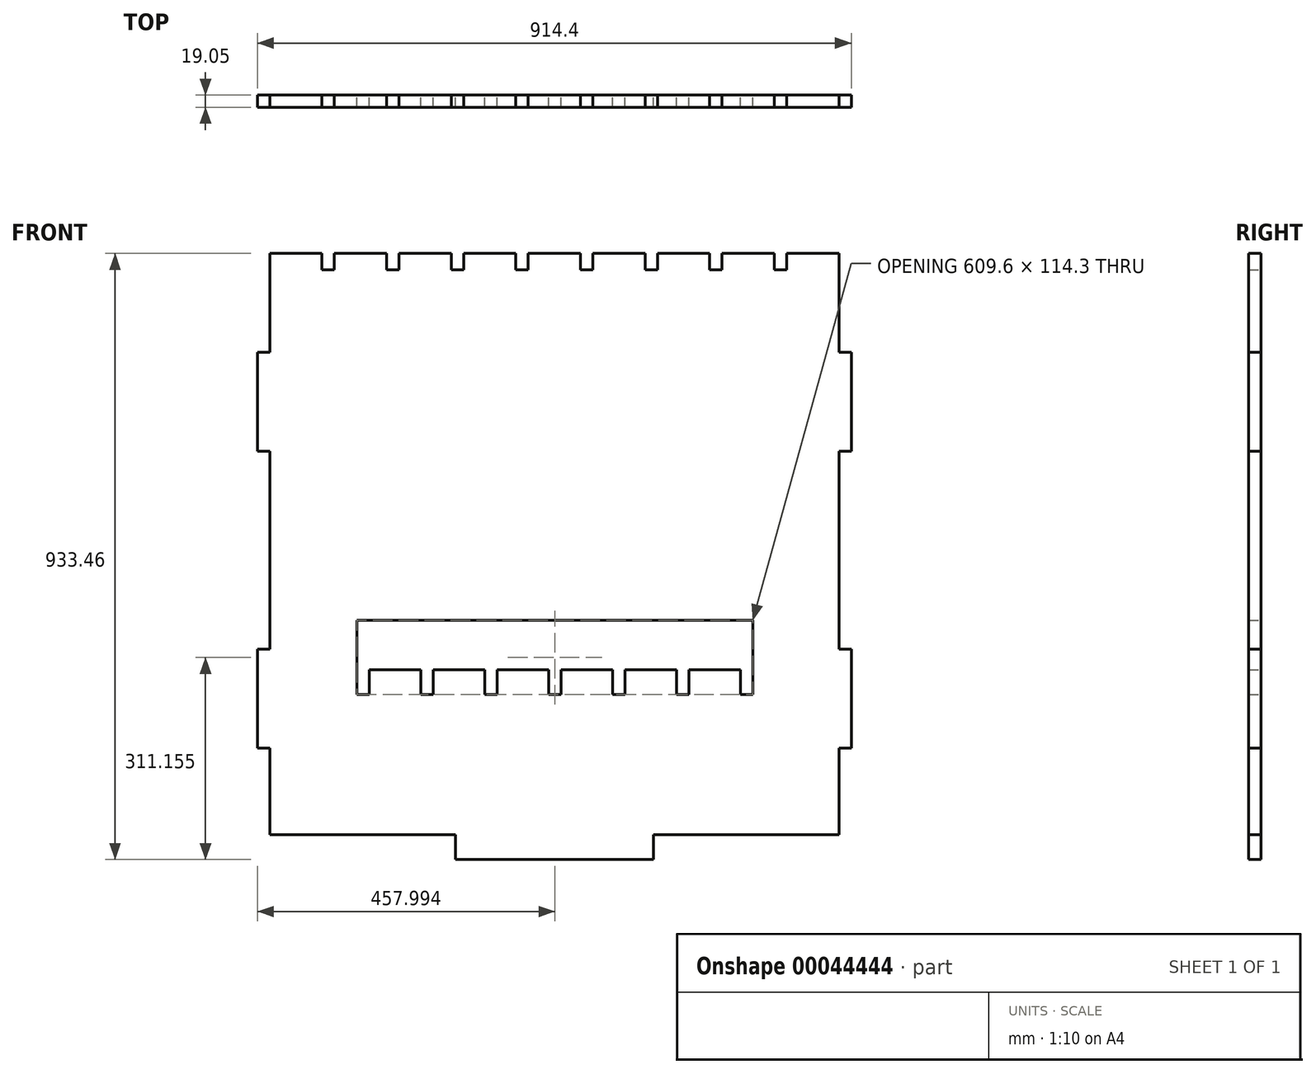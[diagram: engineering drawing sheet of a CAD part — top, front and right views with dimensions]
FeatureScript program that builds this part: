
annotation { "Feature Type Name" : "Feature", "Feature Type Description" : "" }
export const myFeature = defineFeature(function(context is Context, id is Id, definition is map)
    precondition{}
    {
        {
            var Q0;
            Q0=qCreatedBy(makeId("Front.planeOp"),FACE);
            var sketch = newSketch(context, id + "F0", { "sketchPlane" : qUnion([Q0])});
            skLineSegment(sketch, "E0.rect.bottom", {"start": v(-438.15, -447.68) * mm, "end": v(438.15, -447.67) * mm});
            skLineSegment(sketch, "E0.rect.top", {"start": v(-438.15, 447.67) * mm, "end": v(438.15, 447.68) * mm});
            skLineSegment(sketch, "E0.rect.left", {"start": v(-438.15, -447.68) * mm, "end": v(-438.15, 447.67) * mm});
            skLineSegment(sketch, "E0.rect.right", {"start": v(438.15, -447.67) * mm, "end": v(438.15, 447.68) * mm});
            skPoint(sketch, "E0.rect.middle", {"position": v(0, 0) * mm});
            skLineSegment(sketch, "E1.bottom", {"start": v(-304, -117.48) * mm, "end": v(305.6, -117.47) * mm});
            skLineSegment(sketch, "E1.left", {"start": v(-304, -117.48) * mm, "end": v(-304, -193.68) * mm});
            skLineSegment(sketch, "E1.right", {"start": v(305.6, -117.47) * mm, "end": v(305.6, -193.67) * mm});
            skLineSegment(sketch, "E2.bottom", {"start": v(-438.15, 295.27) * mm, "end": v(-457.2, 295.27) * mm});
            skLineSegment(sketch, "E2.top", {"start": v(-438.15, 142.87) * mm, "end": v(-457.2, 142.87) * mm});
            skLineSegment(sketch, "E2.left", {"start": v(-438.15, 295.27) * mm, "end": v(-438.15, 142.87) * mm});
            skLineSegment(sketch, "E2.right", {"start": v(-457.2, 295.27) * mm, "end": v(-457.2, 142.87) * mm});
            skLineSegment(sketch, "E3.bottom", {"start": v(-438.15, -161.93) * mm, "end": v(-457.2, -161.93) * mm});
            skLineSegment(sketch, "E3.top", {"start": v(-438.15, -314.33) * mm, "end": v(-457.2, -314.33) * mm});
            skLineSegment(sketch, "E3.left", {"start": v(-438.15, -161.93) * mm, "end": v(-438.15, -314.33) * mm});
            skLineSegment(sketch, "E3.right", {"start": v(-457.2, -161.93) * mm, "end": v(-457.2, -314.33) * mm});
            skLineSegment(sketch, "E4.bottom", {"start": v(-152.4, -447.68) * mm, "end": v(152.4, -447.67) * mm});
            skLineSegment(sketch, "E4.top", {"start": v(-152.4, -485.78) * mm, "end": v(152.4, -485.77) * mm});
            skLineSegment(sketch, "E4.left", {"start": v(-152.4, -447.68) * mm, "end": v(-152.4, -485.78) * mm});
            skLineSegment(sketch, "E5.MirrorCS", {"start": v(438.15, 142.88) * mm, "end": v(457.2, 142.88) * mm});
            skLineSegment(sketch, "E6.MirrorCS", {"start": v(438.15, 295.28) * mm, "end": v(457.2, 295.28) * mm});
            skLineSegment(sketch, "E7.MirrorCS", {"start": v(438.15, 295.27) * mm, "end": v(438.15, 142.87) * mm});
            skLineSegment(sketch, "E8.MirrorCS", {"start": v(457.2, 295.27) * mm, "end": v(457.2, 142.87) * mm});
            skLineSegment(sketch, "E9.MirrorCS", {"start": v(457.2, -161.93) * mm, "end": v(457.2, -314.33) * mm});
            skLineSegment(sketch, "E10.MirrorCS", {"start": v(438.15, -161.93) * mm, "end": v(438.15, -314.33) * mm});
            skLineSegment(sketch, "E11.MirrorCS", {"start": v(438.15, -161.92) * mm, "end": v(457.2, -161.92) * mm});
            skLineSegment(sketch, "E12.MirrorCS", {"start": v(438.15, -314.32) * mm, "end": v(457.2, -314.32) * mm});
            skLineSegment(sketch, "E13.MirrorCS", {"start": v(152.4, -447.68) * mm, "end": v(152.4, -485.78) * mm});
            skLineSegment(sketch, "E14.MirrorCS", {"start": v(152.4, -447.67) * mm, "end": v(-152.4, -447.68) * mm});
            skLineSegment(sketch, "E15.MirrorCS", {"start": v(152.4, -485.77) * mm, "end": v(-152.4, -485.78) * mm});
            skLineSegment(sketch, "E16.bottom", {"start": v(-205.58, -193.68) * mm, "end": v(-186.53, -193.68) * mm});
            skLineSegment(sketch, "E16.top", {"start": v(-205.58, -231.77) * mm, "end": v(-186.53, -231.77) * mm});
            skLineSegment(sketch, "E16.left", {"start": v(-205.58, -193.68) * mm, "end": v(-205.58, -231.78) * mm});
            skLineSegment(sketch, "E16.right", {"start": v(-186.53, -193.68) * mm, "end": v(-186.53, -231.78) * mm});
            skLineSegment(sketch, "E17.bottom", {"start": v(-107.16, -193.67) * mm, "end": v(-88.1, -193.67) * mm});
            skLineSegment(sketch, "E17.top", {"start": v(-107.16, -231.77) * mm, "end": v(-88.1, -231.77) * mm});
            skLineSegment(sketch, "E17.left", {"start": v(-107.16, -193.68) * mm, "end": v(-107.16, -231.78) * mm});
            skLineSegment(sketch, "E17.right", {"start": v(-88.1, -193.68) * mm, "end": v(-88.1, -231.78) * mm});
            skLineSegment(sketch, "E18.bottom", {"start": v(-8.73, -193.67) * mm, "end": v(10.32, -193.67) * mm});
            skLineSegment(sketch, "E18.top", {"start": v(-8.73, -231.77) * mm, "end": v(10.32, -231.77) * mm});
            skLineSegment(sketch, "E18.left", {"start": v(-8.73, -193.68) * mm, "end": v(-8.73, -231.78) * mm});
            skLineSegment(sketch, "E18.right", {"start": v(10.32, -193.68) * mm, "end": v(10.32, -231.78) * mm});
            skLineSegment(sketch, "E19.bottom", {"start": v(89.7, -193.67) * mm, "end": v(108.74, -193.67) * mm});
            skLineSegment(sketch, "E19.top", {"start": v(89.7, -231.77) * mm, "end": v(108.74, -231.77) * mm});
            skLineSegment(sketch, "E19.left", {"start": v(89.7, -193.68) * mm, "end": v(89.7, -231.78) * mm});
            skLineSegment(sketch, "E19.right", {"start": v(108.74, -193.68) * mm, "end": v(108.74, -231.78) * mm});
            skLineSegment(sketch, "E20.bottom", {"start": v(188.12, -193.67) * mm, "end": v(207.17, -193.67) * mm});
            skLineSegment(sketch, "E20.top", {"start": v(188.12, -231.77) * mm, "end": v(207.17, -231.77) * mm});
            skLineSegment(sketch, "E20.left", {"start": v(188.12, -193.67) * mm, "end": v(188.12, -231.78) * mm});
            skLineSegment(sketch, "E20.right", {"start": v(207.17, -193.67) * mm, "end": v(207.17, -231.78) * mm});
            skLineSegment(sketch, "E21", {"start": v(-304, -193.68) * mm, "end": v(305.6, -193.67) * mm});
            skLineSegment(sketch, "E22.top", {"start": v(40.22, 422.27) * mm, "end": v(59.27, 422.27) * mm});
            skLineSegment(sketch, "E23.right", {"start": v(-338.67, 447.67) * mm, "end": v(-338.67, 422.27) * mm});
            skLineSegment(sketch, "E24.left", {"start": v(139.7, 447.68) * mm, "end": v(139.7, 422.27) * mm});
            skLineSegment(sketch, "E24.top", {"start": v(139.7, 422.27) * mm, "end": v(158.75, 422.27) * mm});
            skLineSegment(sketch, "E24.right", {"start": v(158.75, 447.68) * mm, "end": v(158.75, 422.27) * mm});
            skLineSegment(sketch, "E25.top", {"start": v(338.67, 422.27) * mm, "end": v(357.72, 422.27) * mm});
            skLineSegment(sketch, "E26.left", {"start": v(-258.23, 447.67) * mm, "end": v(-258.23, 422.27) * mm});
            skLineSegment(sketch, "E22.right", {"start": v(59.27, 447.68) * mm, "end": v(59.27, 422.27) * mm});
            skLineSegment(sketch, "E27.top", {"start": v(239.18, 422.27) * mm, "end": v(258.23, 422.27) * mm});
            skLineSegment(sketch, "E28.top", {"start": v(-158.75, 422.27) * mm, "end": v(-139.7, 422.27) * mm});
            skLineSegment(sketch, "E26.top", {"start": v(-258.23, 422.27) * mm, "end": v(-239.18, 422.27) * mm});
            skLineSegment(sketch, "E22.left", {"start": v(40.22, 447.68) * mm, "end": v(40.22, 422.27) * mm});
            skLineSegment(sketch, "E23.top", {"start": v(-357.72, 422.27) * mm, "end": v(-338.67, 422.27) * mm});
            skLineSegment(sketch, "E25.left", {"start": v(338.67, 447.68) * mm, "end": v(338.67, 422.27) * mm});
            skLineSegment(sketch, "E26.right", {"start": v(-239.18, 447.68) * mm, "end": v(-239.18, 422.27) * mm});
            skLineSegment(sketch, "E29.right", {"start": v(-40.22, 447.68) * mm, "end": v(-40.22, 422.27) * mm});
            skLineSegment(sketch, "E27.left", {"start": v(239.18, 447.68) * mm, "end": v(239.18, 422.27) * mm});
            skLineSegment(sketch, "E28.left", {"start": v(-158.75, 447.68) * mm, "end": v(-158.75, 422.27) * mm});
            skLineSegment(sketch, "E29.top", {"start": v(-59.27, 422.27) * mm, "end": v(-40.22, 422.27) * mm});
            skLineSegment(sketch, "E23.left", {"start": v(-357.72, 447.67) * mm, "end": v(-357.72, 422.27) * mm});
            skLineSegment(sketch, "E25.right", {"start": v(357.72, 447.68) * mm, "end": v(357.72, 422.27) * mm});
            skLineSegment(sketch, "E29.left", {"start": v(-59.27, 447.68) * mm, "end": v(-59.27, 422.27) * mm});
            skLineSegment(sketch, "E27.right", {"start": v(258.23, 447.68) * mm, "end": v(258.23, 422.27) * mm});
            skLineSegment(sketch, "E28.right", {"start": v(-139.7, 447.68) * mm, "end": v(-139.7, 422.27) * mm});
            skLineSegment(sketch, "E30.bottom", {"start": v(-304, -193.68) * mm, "end": v(-284.96, -193.68) * mm});
            skLineSegment(sketch, "E30.top", {"start": v(-304, -231.78) * mm, "end": v(-284.96, -231.78) * mm});
            skLineSegment(sketch, "E30.left", {"start": v(-304, -193.68) * mm, "end": v(-304, -231.78) * mm});
            skLineSegment(sketch, "E30.right", {"start": v(-284.96, -193.68) * mm, "end": v(-284.96, -231.78) * mm});
            skLineSegment(sketch, "E31.bottom", {"start": v(305.6, -193.67) * mm, "end": v(286.54, -193.67) * mm});
            skLineSegment(sketch, "E31.top", {"start": v(305.6, -231.77) * mm, "end": v(286.54, -231.77) * mm});
            skLineSegment(sketch, "E31.left", {"start": v(305.6, -193.67) * mm, "end": v(305.6, -231.77) * mm});
            skLineSegment(sketch, "E31.right", {"start": v(286.54, -193.67) * mm, "end": v(286.54, -231.77) * mm});
            skSolve(sketch);
        }
        {
            var Q0;
            {var subQ4=sQuery(id+"F0.wireOp",EDGE,"E0.rect.top");Q0=makeQuery(id+"F0.imprint","IMPRINT",FACE,{"disambiguationData":[TD([[makeQuery(id+"F0.imprint","IMPRINT",EDGE,{"derivedFrom":subQ4}),-1.0]])]});}
            var Q1;
            Q1=makeQuery(id+"F0.imprint","IMPRINT",FACE,{"disambiguationData":[TD([[makeQuery(id+"F0.imprint","IMPRINT",EDGE,{"derivedFrom":sQuery(id+"F0.wireOp",EDGE,"E2.bottom")}),1.0]])]});
            var Q2;
            Q2=makeQuery(id+"F0.imprint","IMPRINT",FACE,{"disambiguationData":[TD([[makeQuery(id+"F0.imprint","IMPRINT",EDGE,{"derivedFrom":sQuery(id+"F0.wireOp",EDGE,"E3.bottom")}),1.0]])]});
            var Q3;
            Q3=makeQuery(id+"F0.imprint","IMPRINT",FACE,{"disambiguationData":[TD([[makeQuery(id+"F0.imprint","IMPRINT",EDGE,{"derivedFrom":sQuery(id+"F0.wireOp",EDGE,"E4.bottom")}),-1.0]])]});
            var Q4;
            Q4=makeQuery(id+"F0.imprint","IMPRINT",FACE,{"disambiguationData":[TD([[makeQuery(id+"F0.imprint","IMPRINT",EDGE,{"derivedFrom":sQuery(id+"F0.wireOp",EDGE,"E13.MirrorCS")}),-1.0]])]});
            var Q5;
            Q5=makeQuery(id+"F0.imprint","IMPRINT",FACE,{"disambiguationData":[TD([[makeQuery(id+"F0.imprint","IMPRINT",EDGE,{"derivedFrom":sQuery(id+"F0.wireOp",EDGE,"E9.MirrorCS")}),-1.0]])]});
            var Q6;
            Q6=makeQuery(id+"F0.imprint","IMPRINT",FACE,{"disambiguationData":[TD([[makeQuery(id+"F0.imprint","IMPRINT",EDGE,{"derivedFrom":sQuery(id+"F0.wireOp",EDGE,"E5.MirrorCS")}),1.0]])]});
            extrude(context, id + "F1", {"entities" : qUnion([Q0, Q1, Q2, Q3, Q4, Q5, Q6]), "depth" : 19.05 * mm});
        }
    });
